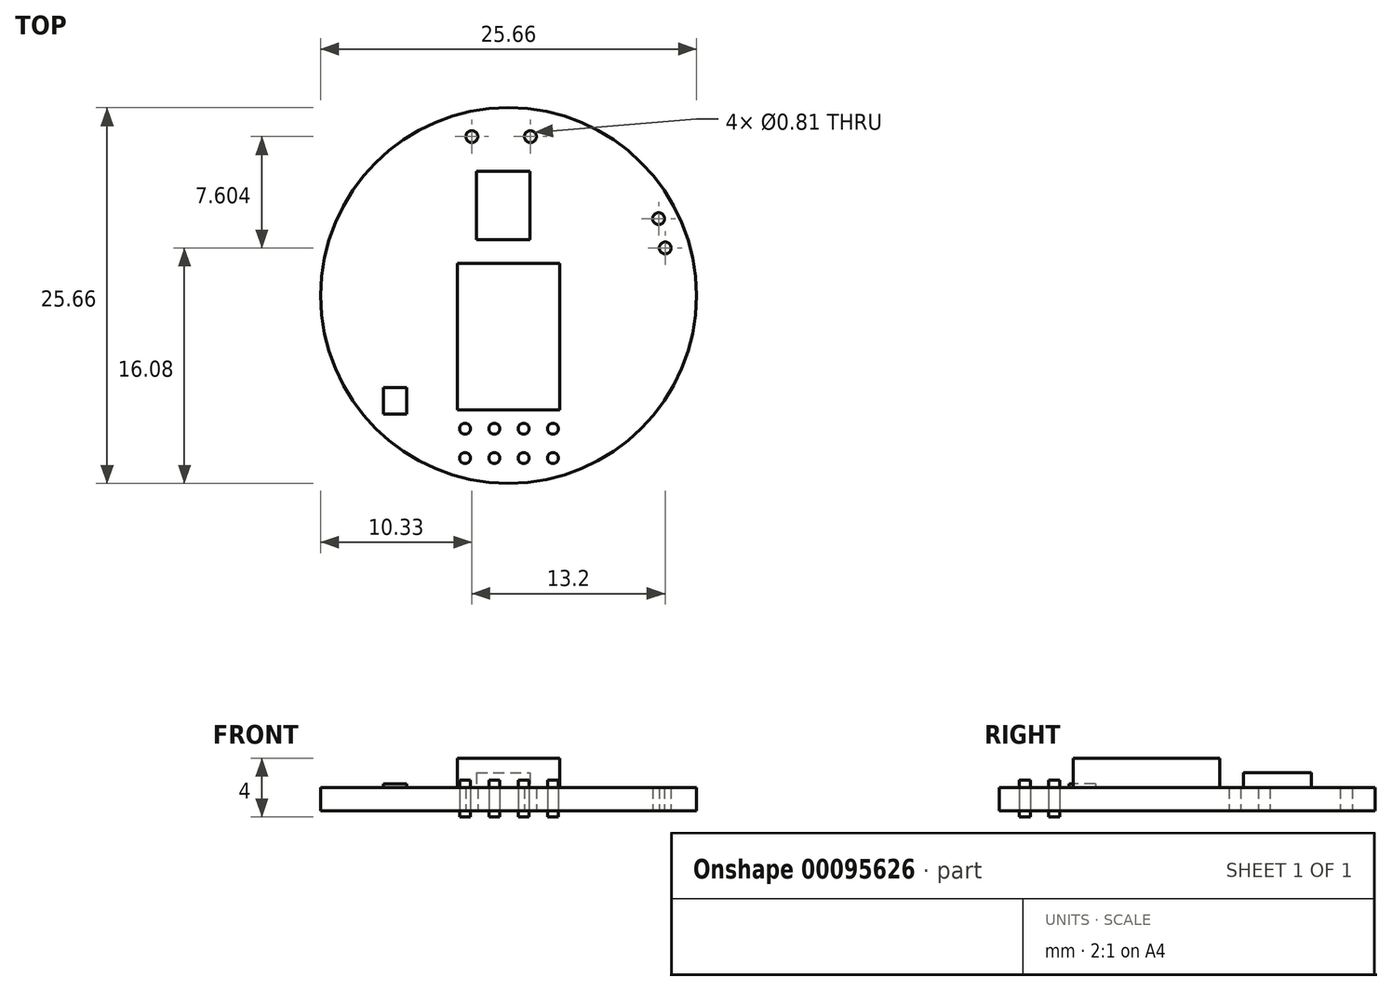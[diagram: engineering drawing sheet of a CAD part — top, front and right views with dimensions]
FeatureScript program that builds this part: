
annotation { "Feature Type Name" : "Feature", "Feature Type Description" : "" }
export const myFeature = defineFeature(function(context is Context, id is Id, definition is map)
    precondition{}
    {
        {
            var Q0;
            Q0=qCreatedBy(makeId("Top.planeOp"),FACE);
            var sketch = newSketch(context, id + "F0", { "sketchPlane" : qUnion([Q0])});
            skCircle(sketch, "E0", {"center": v(0, 0) * mm, "radius": 12.83 * mm});
            skCircle(sketch, "E1", {"center": v(-2.5, 10.85) * mm, "radius": 0.4 * mm});
            skCircle(sketch, "E2", {"center": v(1.5, 10.85) * mm, "radius": 0.4 * mm});
            skCircle(sketch, "E3", {"center": v(10.25, 5.25) * mm, "radius": 0.4 * mm});
            skCircle(sketch, "E4", {"center": v(10.7, 3.25) * mm, "radius": 0.4 * mm});
            skSolve(sketch);
        }
        {
            var Q0;
            Q0=qSketchRegion(id+"F0",true);
            extrude(context, id + "F1", {"entities" : qUnion([Q0]), "depth" : 1.6 * mm});
        }
        {
            var Q0;
            Q0=makeQuery(id+"F1.opExtrude","CAP_FACE",FACE,{"disambiguationData":[OSD([sQuery(id+"F0.wireOp",EDGE,"E0")])],"isStart":false});
            var sketch = newSketch(context, id + "F2", { "sketchPlane" : qUnion([Q0])});
            skLineSegment(sketch, "E5.bottom", {"start": v(-3.49, 2.2) * mm, "end": v(3.51, 2.2) * mm});
            skLineSegment(sketch, "E5.top", {"start": v(-3.49, -7.8) * mm, "end": v(3.51, -7.8) * mm});
            skLineSegment(sketch, "E5.left", {"start": v(-3.49, 2.2) * mm, "end": v(-3.49, -7.8) * mm});
            skLineSegment(sketch, "E5.right", {"start": v(3.51, 2.2) * mm, "end": v(3.51, -7.8) * mm});
            skSolve(sketch);
        }
        {
            var Q0;
            Q0=qSketchRegion(id+"F2",true);
            extrude(context, id + "F3", {"entities" : qUnion([Q0]), "depth" : 2 * mm});
        }
        {
            var Q0;
            Q0=makeQuery(id+"F1.opExtrude","CAP_FACE",FACE,{"disambiguationData":[OSD([sQuery(id+"F0.wireOp",EDGE,"E0")])],"isStart":false});
            var sketch = newSketch(context, id + "F4", { "sketchPlane" : qUnion([Q0])});
            skLineSegment(sketch, "E6.bottom", {"start": v(-8.54, -6.28) * mm, "end": v(-6.94, -6.28) * mm});
            skLineSegment(sketch, "E6.top", {"start": v(-8.54, -8.08) * mm, "end": v(-6.94, -8.08) * mm});
            skLineSegment(sketch, "E6.left", {"start": v(-8.54, -6.28) * mm, "end": v(-8.54, -8.08) * mm});
            skLineSegment(sketch, "E6.right", {"start": v(-6.94, -6.28) * mm, "end": v(-6.94, -8.08) * mm});
            skSolve(sketch);
        }
        {
            var Q0;
            Q0=qSketchRegion(id+"F4",true);
            extrude(context, id + "F5", {"entities" : qUnion([Q0]), "depth" : .25 * mm});
        }
        {
            var Q0;
            Q0=makeQuery(id+"F1.opExtrude","CAP_FACE",FACE,{"disambiguationData":[OSD([sQuery(id+"F0.wireOp",EDGE,"E0"),sQuery(id+"F0.wireOp",EDGE,"E1"),sQuery(id+"F0.wireOp",EDGE,"E2"),sQuery(id+"F0.wireOp",EDGE,"E3"),sQuery(id+"F0.wireOp",EDGE,"E4")])],"isStart":false});
            var sketch = newSketch(context, id + "F6", { "sketchPlane" : qUnion([Q0])});
            skLineSegment(sketch, "E7.bottom", {"start": v(-2.17, 8.48) * mm, "end": v(1.48, 8.48) * mm});
            skLineSegment(sketch, "E7.top", {"start": v(-2.17, 3.83) * mm, "end": v(1.48, 3.83) * mm});
            skLineSegment(sketch, "E7.left", {"start": v(-2.17, 8.48) * mm, "end": v(-2.17, 3.83) * mm});
            skLineSegment(sketch, "E7.right", {"start": v(1.48, 8.48) * mm, "end": v(1.48, 3.83) * mm});
            skSolve(sketch);
        }
        {
            var Q0;
            Q0=qSketchRegion(id+"F6",true);
            extrude(context, id + "F7", {"entities" : qUnion([Q0]), "depth" : 1 * mm});
        }
        {
            var Q0;
            Q0=makeQuery(id+"F1.opExtrude","CAP_FACE",FACE,{"disambiguationData":[OSD([sQuery(id+"F0.wireOp",EDGE,"E0"),sQuery(id+"F0.wireOp",EDGE,"E1"),sQuery(id+"F0.wireOp",EDGE,"E2"),sQuery(id+"F0.wireOp",EDGE,"E3"),sQuery(id+"F0.wireOp",EDGE,"E4")])],"isStart":false});
            var sketch = newSketch(context, id + "F8", { "sketchPlane" : qUnion([Q0])});
            skCircle(sketch, "E8", {"center": v(-2.96, -9.09) * mm, "radius": 0.38 * mm});
            skCircle(sketch, "E9", {"center": v(-0.96, -9.09) * mm, "radius": 0.38 * mm});
            skCircle(sketch, "E10", {"center": v(1.04, -9.09) * mm, "radius": 0.38 * mm});
            skCircle(sketch, "E11", {"center": v(3.04, -9.09) * mm, "radius": 0.38 * mm});
            skCircle(sketch, "E12", {"center": v(-2.96, -11.09) * mm, "radius": 0.38 * mm});
            skCircle(sketch, "E13", {"center": v(-0.96, -11.09) * mm, "radius": 0.38 * mm});
            skCircle(sketch, "E14", {"center": v(1.04, -11.09) * mm, "radius": 0.38 * mm});
            skCircle(sketch, "E15", {"center": v(3.04, -11.09) * mm, "radius": 0.38 * mm});
            skSolve(sketch);
        }
        {
            var Q0;
            Q0=makeQuery(id+"F8.imprint","IMPRINT",FACE,{"disambiguationData":[TD([[makeQuery(id+"F8.imprint","IMPRINT",EDGE,{"derivedFrom":sQuery(id+"F8.wireOp",EDGE,"E8")}),1.0]])]});
            var Q1;
            Q1=makeQuery(id+"F8.imprint","IMPRINT",FACE,{"disambiguationData":[TD([[makeQuery(id+"F8.imprint","IMPRINT",EDGE,{"derivedFrom":sQuery(id+"F8.wireOp",EDGE,"E9")}),1.0]])]});
            var Q2;
            Q2=makeQuery(id+"F8.imprint","IMPRINT",FACE,{"disambiguationData":[TD([[makeQuery(id+"F8.imprint","IMPRINT",EDGE,{"derivedFrom":sQuery(id+"F8.wireOp",EDGE,"E10")}),1.0]])]});
            var Q3;
            Q3=makeQuery(id+"F8.imprint","IMPRINT",FACE,{"disambiguationData":[TD([[makeQuery(id+"F8.imprint","IMPRINT",EDGE,{"derivedFrom":sQuery(id+"F8.wireOp",EDGE,"E11")}),1.0]])]});
            var Q4;
            Q4=makeQuery(id+"F8.imprint","IMPRINT",FACE,{"disambiguationData":[TD([[makeQuery(id+"F8.imprint","IMPRINT",EDGE,{"derivedFrom":sQuery(id+"F8.wireOp",EDGE,"E12")}),1.0]])]});
            var Q5;
            Q5=makeQuery(id+"F8.imprint","IMPRINT",FACE,{"disambiguationData":[TD([[makeQuery(id+"F8.imprint","IMPRINT",EDGE,{"derivedFrom":sQuery(id+"F8.wireOp",EDGE,"E13")}),1.0]])]});
            var Q6;
            Q6=makeQuery(id+"F8.imprint","IMPRINT",FACE,{"disambiguationData":[TD([[makeQuery(id+"F8.imprint","IMPRINT",EDGE,{"derivedFrom":sQuery(id+"F8.wireOp",EDGE,"E14")}),1.0]])]});
            var Q7;
            Q7=makeQuery(id+"F8.imprint","IMPRINT",FACE,{"disambiguationData":[TD([[makeQuery(id+"F8.imprint","IMPRINT",EDGE,{"derivedFrom":sQuery(id+"F8.wireOp",EDGE,"E15")}),1.0]])]});
            extrude(context, id + "F9", {"entities" : qUnion([Q0, Q1, Q2, Q3, Q4, Q5, Q6, Q7]), "depth" : .5 * mm, "hasSecondDirection" : true, "secondDirectionOppositeDirection" : true, "secondDirectionDepth" : 2 * mm});
        }
    });
